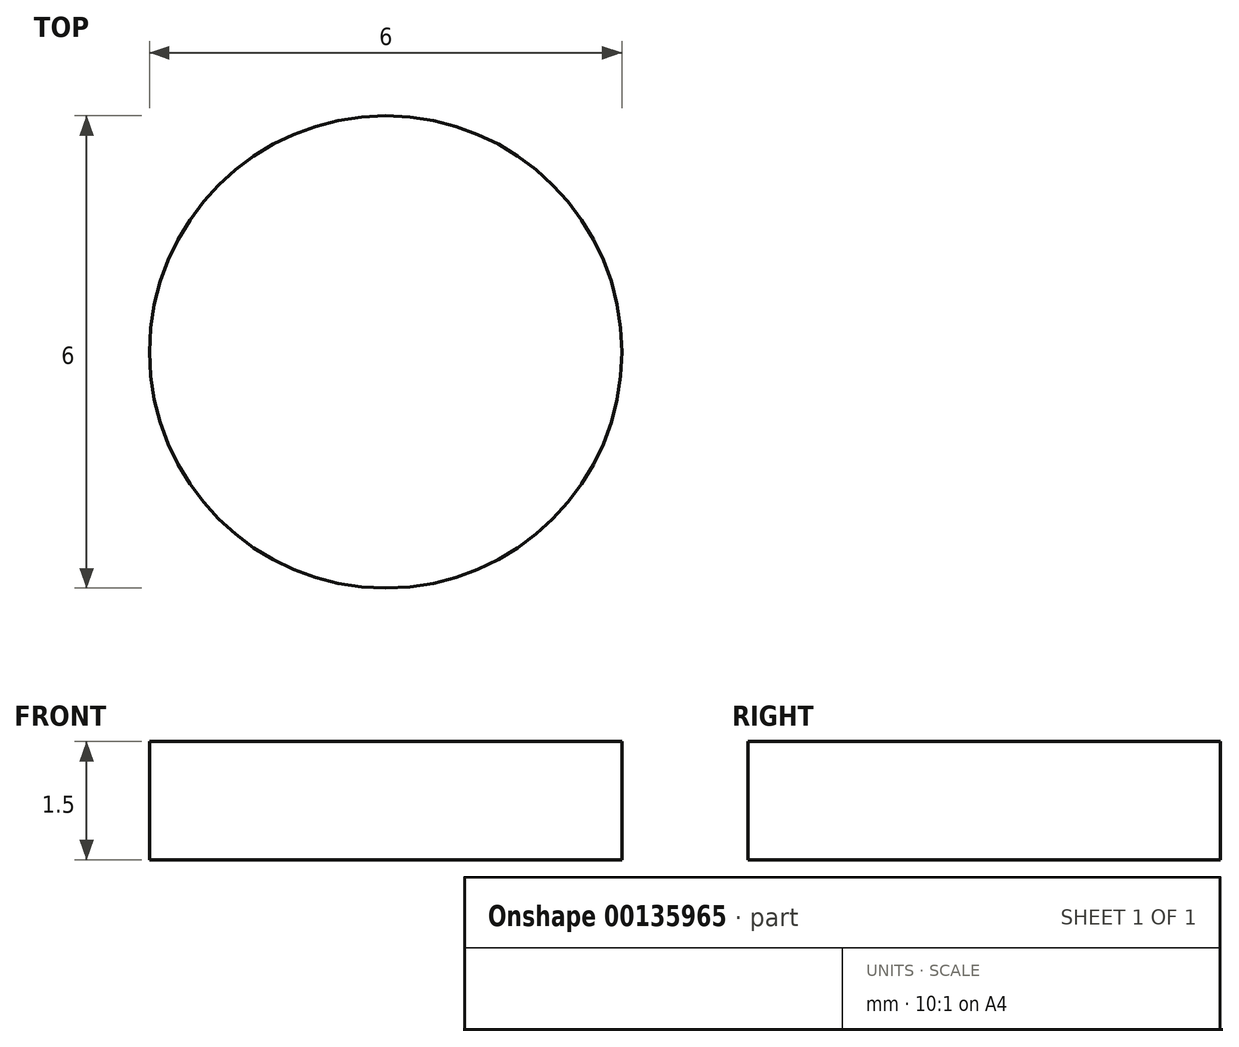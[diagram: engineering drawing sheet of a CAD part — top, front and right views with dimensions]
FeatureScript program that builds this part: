
annotation { "Feature Type Name" : "Feature", "Feature Type Description" : "" }
export const myFeature = defineFeature(function(context is Context, id is Id, definition is map)
    precondition{}
    {
        {
            var Q0;
            Q0=qCreatedBy(makeId("Top.planeOp"),FACE);
            var sketch = newSketch(context, id + "F0", { "sketchPlane" : qUnion([Q0])});
            skCircle(sketch, "E0", {"center": v(0, 0) * mm, "radius": 3 * mm});
            skSolve(sketch);
        }
        {
            var Q0;
            Q0=qSketchRegion(id+"F0",true);
            extrude(context, id + "F1", {"entities" : qUnion([Q0]), "depth" : 1.5 * mm});
        }
    });
